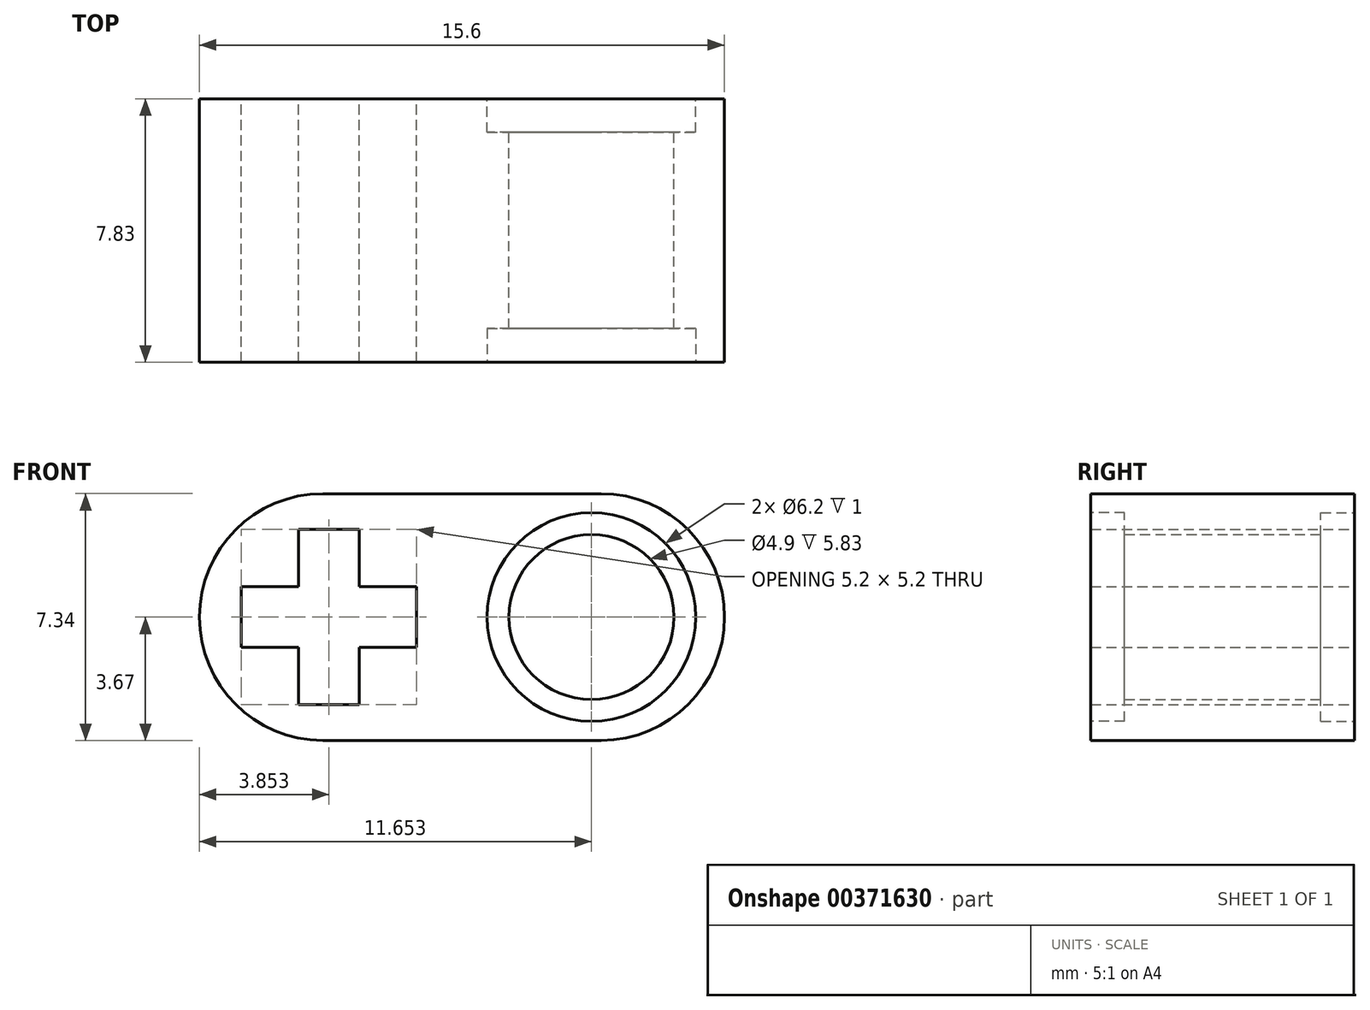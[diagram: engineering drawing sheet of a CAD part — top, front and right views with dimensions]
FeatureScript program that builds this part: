
annotation { "Feature Type Name" : "Feature", "Feature Type Description" : "" }
export const myFeature = defineFeature(function(context is Context, id is Id, definition is map)
    precondition{}
    {
        {
            var Q0;
            Q0=qCreatedBy(makeId("Front.planeOp"),FACE);
            var sketch = newSketch(context, id + "F0", { "sketchPlane" : qUnion([Q0])});
            skLineSegment(sketch, "E0", {"start": v(-0.42, -3.67) * mm, "end": v(7.85, -3.67) * mm});
            skLineSegment(sketch, "E1", {"start": v(11.51, -3.67) * mm, "end": v(3.61, -3.67) * mm, "construction": true});
            skLineSegment(sketch, "E2", {"start": v(11.51, 0) * mm, "end": v(11.51, 0) * mm});
            skLineSegment(sketch, "E3", {"start": v(-11.99, 0) * mm, "end": v(11.51, 0) * mm, "construction": true});
            skLineSegment(sketch, "E4", {"start": v(7.85, 3.67) * mm, "end": v(3.61, 3.67) * mm});
            skLineSegment(sketch, "E5", {"start": v(3.61, 3.66) * mm, "end": v(-0.42, 3.67) * mm});
            skLineSegment(sketch, "E6", {"start": v(-11.99, 0) * mm, "end": v(-11.99, 0) * mm});
            skLineSegment(sketch, "E7", {"start": v(3.61, 3.67) * mm, "end": v(3.61, -3.66) * mm, "construction": true});
            skLineSegment(sketch, "E8", {"start": v(-8.04, -3.66) * mm, "end": v(-8.04, 3.67) * mm, "construction": true});
            skLineSegment(sketch, "E9", {"start": v(-0.24, 3.67) * mm, "end": v(-0.24, -4.32) * mm, "construction": true});
            skLineSegment(sketch, "E10", {"start": v(7.56, 3.67) * mm, "end": v(7.56, -3.66) * mm, "construction": true});
            skPoint(sketch, "E11.visualSharp", {"position": v(-11.99, 3.67) * mm});
            skPoint(sketch, "E12.visualSharp", {"position": v(-11.99, -3.67) * mm});
            skPoint(sketch, "E13.visualSharp", {"position": v(11.51, 3.67) * mm});
            skArc(sketch, "E13.filletArc", {"start": v(11.51, 0) * mm, "mid": v(10.44, 2.6) * mm, "end": v(7.85, 3.66) * mm});
            skPoint(sketch, "E14.visualSharp", {"position": v(11.51, -3.67) * mm});
            skArc(sketch, "E14.filletArc", {"start": v(7.85, -3.67) * mm, "mid": v(10.44, -2.6) * mm, "end": v(11.51, 0) * mm});
            skCircle(sketch, "E15", {"center": v(7.56, 0) * mm, "radius": 2.45 * mm});
            skArc(sketch, "E16", {"start": v(5.98, 2.67) * mm, "mid": v(4.46, 0) * mm, "end": v(5.98, -2.66) * mm});
            skArc(sketch, "E17", {"start": v(5.98, -2.66) * mm, "mid": v(10.66, 0) * mm, "end": v(5.98, 2.67) * mm});
            skLineSegment(sketch, "E18", {"start": v(-4.09, 0) * mm, "end": v(-4.09, 0) * mm});
            skPoint(sketch, "E19.newPointB", {"position": v(-4.09, -3.66) * mm});
            skArc(sketch, "E19.filletArc", {"start": v(-4.09, 0) * mm, "mid": v(-3.01, -2.6) * mm, "end": v(-0.42, -3.66) * mm});
            skPoint(sketch, "E20.visualSharp", {"position": v(-4.09, 3.67) * mm});
            skArc(sketch, "E20.filletArc", {"start": v(-0.42, 3.67) * mm, "mid": v(-3.01, 2.6) * mm, "end": v(-4.09, 0) * mm});
            skLineSegment(sketch, "E21", {"start": v(-4.09, 0) * mm, "end": v(11.51, 0) * mm});
            skLineSegment(sketch, "E22", {"start": v(-0.24, 0) * mm, "end": v(-0.24, 2.6) * mm});
            skLineSegment(sketch, "E23", {"start": v(-0.24, 2.6) * mm, "end": v(-1.14, 2.6) * mm});
            skLineSegment(sketch, "E24", {"start": v(-1.14, 2.6) * mm, "end": v(-1.14, 0.9) * mm});
            skLineSegment(sketch, "E25", {"start": v(-1.14, 0.9) * mm, "end": v(-2.84, 0.9) * mm});
            skLineSegment(sketch, "E26", {"start": v(-2.84, 0.9) * mm, "end": v(-2.84, 0) * mm});
            skLineSegment(sketch, "E27.MirrorCS", {"start": v(-1.14, -0.9) * mm, "end": v(-2.84, -0.9) * mm});
            skLineSegment(sketch, "E28.MirrorCS", {"start": v(-2.84, -0.9) * mm, "end": v(-2.84, 0) * mm});
            skLineSegment(sketch, "E29.MirrorCS", {"start": v(-1.14, -2.6) * mm, "end": v(-1.14, -0.9) * mm});
            skLineSegment(sketch, "E30.MirrorCS", {"start": v(-0.24, -2.6) * mm, "end": v(-1.14, -2.6) * mm});
            skLineSegment(sketch, "E31.MirrorCS", {"start": v(-0.24, -2.6) * mm, "end": v(0.66, -2.6) * mm});
            skLineSegment(sketch, "E32.MirrorCS", {"start": v(0.66, -2.6) * mm, "end": v(0.66, -0.9) * mm});
            skLineSegment(sketch, "E33.MirrorCS", {"start": v(0.66, -0.9) * mm, "end": v(2.36, -0.9) * mm});
            skLineSegment(sketch, "E34.MirrorCS", {"start": v(2.36, -0.9) * mm, "end": v(2.36, 0) * mm});
            skLineSegment(sketch, "E35.MirrorCS", {"start": v(2.36, 0.9) * mm, "end": v(2.36, 0) * mm});
            skLineSegment(sketch, "E36.MirrorCS", {"start": v(0.66, 0.9) * mm, "end": v(2.36, 0.9) * mm});
            skLineSegment(sketch, "E37.MirrorCS", {"start": v(0.66, 2.6) * mm, "end": v(0.66, 0.9) * mm});
            skLineSegment(sketch, "E38.MirrorCS", {"start": v(-0.24, 2.6) * mm, "end": v(0.66, 2.6) * mm});
            skSolve(sketch);
        }
        {
            var Q0;
            Q0=makeQuery(id+"F0.imprint","IMPRINT",FACE,{"disambiguationData":[TD([[makeQuery(id+"F0.imprint","IMPRINT",EDGE,{"derivedFrom":sQuery(id+"F0.wireOp",EDGE,"3114418e-8a23-436a-bf6c-323d072f051f")}),-1.0]])]});
            var Q1;
            Q1=makeQuery(id+"F0.imprint","IMPRINT",FACE,{"disambiguationData":[TD([[makeQuery(id+"F0.imprint","IMPRINT",EDGE,{"derivedFrom":sQuery(id+"F0.wireOp",EDGE,"E4")}),1.0]])]});
            var Q2;
            Q2=makeQuery(id+"F0.imprint","IMPRINT",FACE,{"disambiguationData":[TD([[makeQuery(id+"F0.imprint","IMPRINT",EDGE,{"derivedFrom":sQuery(id+"F0.wireOp",EDGE,"E0")}),1.0]])]});
            var Q3;
            {var subQ0=sQuery(id+"F0.wireOp",EDGE,"E21");var subQ1=sQuery(id+"F0.wireOp",EDGE,"E15");var subQ2=makeQuery(id+"F0.imprint","INTERSECT",VERTEX,{"disambiguationData":[OD(0.0)],"derivedFrom":[subQ1,subQ0]});Q3=makeQuery(id+"F0.imprint","IMPRINT",FACE,{"disambiguationData":[TD([[makeQuery(id+"F0.imprint","IMPRINT",EDGE,{"disambiguationData":[TD([[subQ2,-1.0]])],"derivedFrom":subQ1}),-1.0]])]});}
            var Q4;
            {var subQ0=sQuery(id+"F0.wireOp",EDGE,"E21");var subQ1=sQuery(id+"F0.wireOp",EDGE,"E15");var subQ2=makeQuery(id+"F0.imprint","INTERSECT",VERTEX,{"disambiguationData":[OD(0.0)],"derivedFrom":[subQ1,subQ0]});Q4=makeQuery(id+"F0.imprint","IMPRINT",FACE,{"disambiguationData":[TD([[makeQuery(id+"F0.imprint","IMPRINT",EDGE,{"disambiguationData":[TD([[subQ2,1.0]])],"derivedFrom":subQ1}),-1.0]])]});}
            extrude(context, id + "F1", {"entities" : qUnion([Q0, Q1, Q2, Q3, Q4]), "depth" : 7.83 * mm});
        }
        {
            var Q0;
            Q0=makeQuery(id+"F0.imprint","IMPRINT",FACE,{"disambiguationData":[TD([[makeQuery(id+"F0.imprint","IMPRINT",EDGE,{"derivedFrom":sQuery(id+"F0.wireOp",EDGE,"3114418e-8a23-436a-bf6c-323d072f051f")}),-1.0]])]});
            var Q1;
            Q1=makeQuery(id+"F0.imprint","IMPRINT",FACE,{"disambiguationData":[TD([[makeQuery(id+"F0.imprint","IMPRINT",EDGE,{"derivedFrom":sQuery(id+"F0.wireOp",EDGE,"E15")}),-1.0]])]});
            extrude(context, id + "F2", {"entities" : qUnion([Q0, Q1]), "operationType" : NewBodyOperationType.REMOVE, "depth" : 1 * mm});
        }
        {
            var Q0;
            Q0=makeQuery(id+"F1.opExtrude","CAP_FACE",FACE,{"disambiguationData":[OSD([sQuery(id+"F0.wireOp",EDGE,"E0"),sQuery(id+"F0.wireOp",EDGE,"E4"),sQuery(id+"F0.wireOp",EDGE,"E5"),sQuery(id+"F0.wireOp",EDGE,"E13.filletArc"),sQuery(id+"F0.wireOp",EDGE,"E14.filletArc"),sQuery(id+"F0.wireOp",EDGE,"E15"),sQuery(id+"F0.wireOp",EDGE,"3114418e-8a23-436a-bf6c-323d072f051f"),sQuery(id+"F0.wireOp",EDGE,"E19.filletArc"),sQuery(id+"F0.wireOp",EDGE,"E20.filletArc")])],"isStart":false});
            var sketch = newSketch(context, id + "F3", { "sketchPlane" : qUnion([Q0])});
            skCircle(sketch, "E39", {"center": v(7.56, 0) * mm, "radius": 3.1 * mm});
            skSolve(sketch);
        }
        {
            var Q0;
            Q0=makeQuery(id+"F3.imprint","IMPRINT",FACE,{"disambiguationData":[TD([[makeQuery(id+"F3.imprint","IMPRINT",EDGE,{"derivedFrom":sQuery(id+"F3.wireOp",EDGE,"DLSnQDaz-8F6T-bjer-TDE3-1eCXASQkTJMb")}),1.0]])]});
            var Q1;
            Q1=makeQuery(id+"F3.imprint","IMPRINT",FACE,{"disambiguationData":[TD([[makeQuery(id+"F3.imprint","IMPRINT",EDGE,{"derivedFrom":sQuery(id+"F3.wireOp",EDGE,"E39")}),1.0]])]});
            extrude(context, id + "F4", {"entities" : qUnion([Q0, Q1]), "operationType" : NewBodyOperationType.REMOVE, "oppositeDirection" : true, "depth" : 1 * mm});
        }
    });
